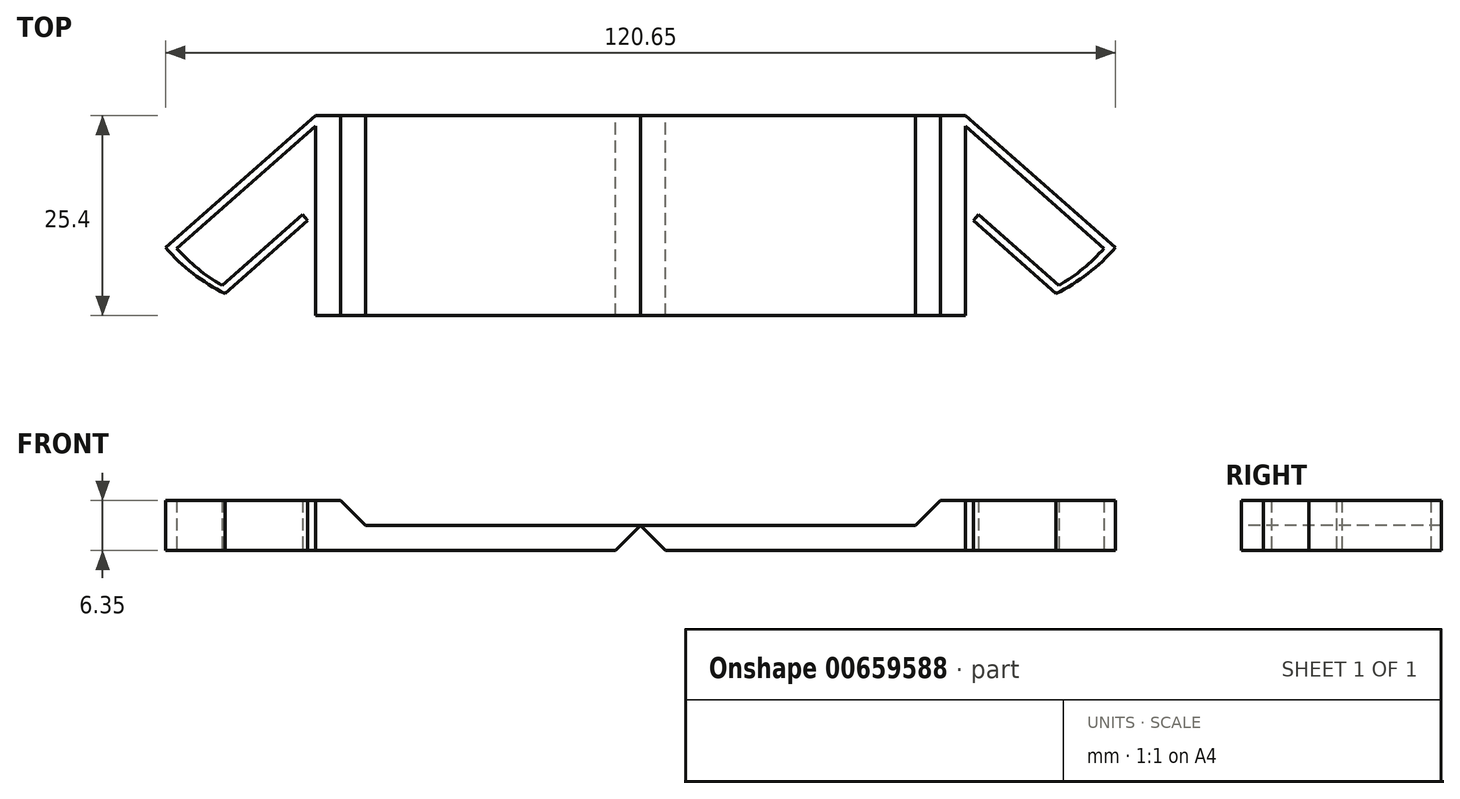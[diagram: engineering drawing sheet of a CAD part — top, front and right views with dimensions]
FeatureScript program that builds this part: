
annotation { "Feature Type Name" : "Feature", "Feature Type Description" : "" }
export const myFeature = defineFeature(function(context is Context, id is Id, definition is map)
    precondition{}
    {
        {
            var Q0;
            Q0=qCreatedBy(makeId("Top.planeOp"),FACE);
            var sketch = newSketch(context, id + "F0", { "sketchPlane" : qUnion([Q0])});
            skLineSegment(sketch, "E0.bottom", {"start": v(28.58, -12.7) * mm, "end": v(-28.58, -12.7) * mm});
            skLineSegment(sketch, "E0.top", {"start": v(28.58, 12.7) * mm, "end": v(-28.58, 12.7) * mm});
            skLineSegment(sketch, "E0.left", {"start": v(28.58, -12.7) * mm, "end": v(28.58, 12.7) * mm});
            skLineSegment(sketch, "E0.right", {"start": v(-28.57, -12.7) * mm, "end": v(-28.57, 12.7) * mm});
            skPoint(sketch, "E0.middle", {"position": v(0, 0) * mm});
            skLineSegment(sketch, "E1", {"start": v(-9.53, 11.37) * mm, "end": v(-9.52, -12.7) * mm});
            skLineSegment(sketch, "E2", {"start": v(0, -12.7) * mm, "end": v(0, 12.7) * mm});
            skPoint(sketch, "E3", {"position": v(-22.22, -12.7) * mm});
            skLineSegment(sketch, "E4", {"start": v(-9.53, 12.7) * mm, "end": v(-28.57, -4.1) * mm});
            skPoint(sketch, "E5", {"position": v(-19.05, -12.7) * mm});
            skArc(sketch, "E6", {"start": v(-28.57, -4.1) * mm, "mid": v(-25.09, -7.37) * mm, "end": v(-21.05, -9.94) * mm});
            skLineSegment(sketch, "E7", {"start": v(-21.05, -9.94) * mm, "end": v(-10.53, -0.66) * mm});
            skLineSegment(sketch, "E8", {"start": v(-10.53, -0.66) * mm, "end": v(-11.19, 0.1) * mm});
            skLineSegment(sketch, "E9", {"start": v(-11.19, 0.1) * mm, "end": v(-11.19, 0.1) * mm});
            skLineSegment(sketch, "E10", {"start": v(-9.53, 11.37) * mm, "end": v(-27.15, -4.18) * mm});
            skArc(sketch, "E11", {"start": v(-27.15, -4.18) * mm, "mid": v(-24.46, -6.77) * mm, "end": v(-21.4, -8.91) * mm});
            skLineSegment(sketch, "E12", {"start": v(-21.4, -8.91) * mm, "end": v(-11.19, 0.1) * mm});
            skSolve(sketch);
        }
        {
            var Q0;
            {var subQ0=sQuery(id+"F0.wireOp",EDGE,"E0.left");Q0=makeQuery(id+"F0.imprint","IMPRINT",FACE,{"disambiguationData":[TD([[makeQuery(id+"F0.imprint","IMPRINT",EDGE,{"derivedFrom":subQ0}),1.0]])]});}
            var Q1;
            {var subQ1=sQuery(id+"F0.wireOp",EDGE,"E1");Q1=makeQuery(id+"F0.imprint","IMPRINT",FACE,{"disambiguationData":[TD([[makeQuery(id+"F0.imprint","IMPRINT",EDGE,{"derivedFrom":subQ1}),1.0]])]});}
            var Q2;
            {var subQ0=sQuery(id+"F0.wireOp",EDGE,"Ll8NUgnO-918t-zldm-zNWz-RsUZQomu35K8");Q2=makeQuery(id+"F0.imprint","IMPRINT",FACE,{"disambiguationData":[TD([[makeQuery(id+"F0.imprint","IMPRINT",EDGE,{"derivedFrom":subQ0}),1.0]])]});}
            extrude(context, id + "F1", {"entities" : qUnion([Q0, Q1, Q2]), "depth" : 3.17 * mm, "offsetDistance" : 25.4 * mm});
        }
        {
            var Q0;
            {var subQ1=sQuery(id+"F0.wireOp",EDGE,"E1");Q0=makeQuery(id+"F0.imprint","IMPRINT",FACE,{"disambiguationData":[TD([[makeQuery(id+"F0.imprint","IMPRINT",EDGE,{"derivedFrom":subQ1}),1.0]])]});}
            extrude(context, id + "F2", {"entities" : qUnion([Q0]), "operationType" : NewBodyOperationType.ADD, "depth" : 6.35 * mm, "offsetDistance" : 25.4 * mm});
        }
        {
            var Q0;
            Q0=makeQuery(id+"F2.opExtrude","CAP_EDGE",EDGE,{"disambiguationData":[OSD([sQuery(id+"F0.wireOp",EDGE,"E2")])],"isStart":false});
            chamfer(context, id + "F3", {"entities" : qUnion([Q0]), "width" : 6.35 * mm, "tangentPropagation" : true});
        }
        {
            var Q0;
            {var subQ0=sQuery(id+"F0.wireOp",EDGE,"E0.left");Q0=makeQuery(id+"F37SAEC6IVc2ddh_1.boolean.opBoolean","MERGE",FACE,{"derivedFrom":[makeQuery(id+"F1.opExtrude","SWEPT_FACE",FACE,{"disambiguationData":[OSD([subQ0])]}),makeQuery(id+"F37SAEC6IVc2ddh_1.opExtrude","SWEPT_FACE",FACE,{"disambiguationData":[OSD([subQ0])]})]});}
            cPlane(context, id + "F4", {"entities" : qUnion([Q0]), "cplaneType" : CPlaneType.OFFSET, "offset" : 3.17 * mm, "width" : 152.4 * mm, "height" : 152.4 * mm});
        }
        {
            var Q0;
            Q0=makeQuery(id+"F1.opExtrude","SWEPT_BODY",BODY,{"disambiguationData":[OSD([sQuery(id+"F0.wireOp",EDGE,"E0.bottom"),sQuery(id+"F0.wireOp",EDGE,"E0.top"),sQuery(id+"F0.wireOp",EDGE,"E0.left"),sQuery(id+"F0.wireOp",EDGE,"E1"),sQuery(id+"F0.wireOp",EDGE,"E4"),sQuery(id+"F0.wireOp",EDGE,"E6"),sQuery(id+"F0.wireOp",EDGE,"E7"),sQuery(id+"F0.wireOp",EDGE,"E8"),sQuery(id+"F0.wireOp",EDGE,"E10"),sQuery(id+"F0.wireOp",EDGE,"E11"),sQuery(id+"F0.wireOp",EDGE,"E12")])]});
            var Q1;
            Q1=qCreatedBy(id+"F4.planeOp",FACE);
            mirror(context, id + "F5", {"entities" : qUnion([Q0]), "mirrorPlane" : qUnion([Q1])});
        }
        {
            var Q0;
            {var subQ0=sQuery(id+"F0.wireOp",EDGE,"E0.bottom");Q0=makeQuery(id+"F2.boolean.opBoolean","MERGE",FACE,{"derivedFrom":[makeQuery(id+"F1.opExtrude","SWEPT_FACE",FACE,{"disambiguationData":[OSD([subQ0])]}),makeQuery(id+"F2.opExtrude","SWEPT_FACE",FACE,{"disambiguationData":[OSD([subQ0])]})]});}
            var sketch = newSketch(context, id + "F6", { "sketchPlane" : qUnion([Q0])});
            skLineSegment(sketch, "E13", {"start": v(28.57, 3.18) * mm, "end": v(31.75, 3.18) * mm});
            skLineSegment(sketch, "E14", {"start": v(31.75, 3.17) * mm, "end": v(28.57, 0) * mm});
            skLineSegment(sketch, "E15", {"start": v(28.57, 0) * mm, "end": v(28.57, 3.18) * mm});
            skLineSegment(sketch, "E16", {"start": v(31.75, 3.18) * mm, "end": v(34.92, 3.18) * mm});
            skLineSegment(sketch, "E17", {"start": v(34.92, 0) * mm, "end": v(31.75, 3.18) * mm});
            skLineSegment(sketch, "E18", {"start": v(34.92, 0) * mm, "end": v(34.92, 3.18) * mm});
            skSolve(sketch);
        }
        {
            var Q0;
            Q0=makeQuery(id+"F6.imprint","IMPRINT",FACE,{"disambiguationData":[TD([[makeQuery(id+"F6.imprint","IMPRINT",EDGE,{"derivedFrom":sQuery(id+"F6.wireOp",EDGE,"E16")}),-1.0]])]});
            var Q1;
            Q1=makeQuery(id+"F6.imprint","IMPRINT",FACE,{"disambiguationData":[TD([[makeQuery(id+"F6.imprint","IMPRINT",EDGE,{"derivedFrom":sQuery(id+"F6.wireOp",EDGE,"E13")}),-1.0]])]});
            var Q2;
            {var subQ0=sQuery(id+"F0.wireOp",EDGE,"E0.bottom");Q2=makeQuery(id+"F5.opPattern","COPY",FACE,{"derivedFrom":makeQuery(id+"F2.boolean.opBoolean","MERGE",FACE,{"derivedFrom":[makeQuery(id+"F1.opExtrude","SWEPT_FACE",FACE,{"disambiguationData":[OSD([subQ0])]}),makeQuery(id+"F2.opExtrude","SWEPT_FACE",FACE,{"disambiguationData":[OSD([subQ0])]})]}),"instanceName":"1"});}
            var Q3;
            Q3=makeQuery(id+"F6.imprint","IMPRINT",FACE,{"disambiguationData":[TD([[makeQuery(id+"F6.imprint","IMPRINT",EDGE,{"derivedFrom":sQuery(id+"F6.wireOp",EDGE,"E15")}),-1.0]])]});
            extrude(context, id + "F7", {"entities" : qUnion([Q0, Q1, Q2, Q3]), "operationType" : NewBodyOperationType.ADD, "oppositeDirection" : true, "depth" : 25.4 * mm, "offsetDistance" : 25.4 * mm});
        }
    });
